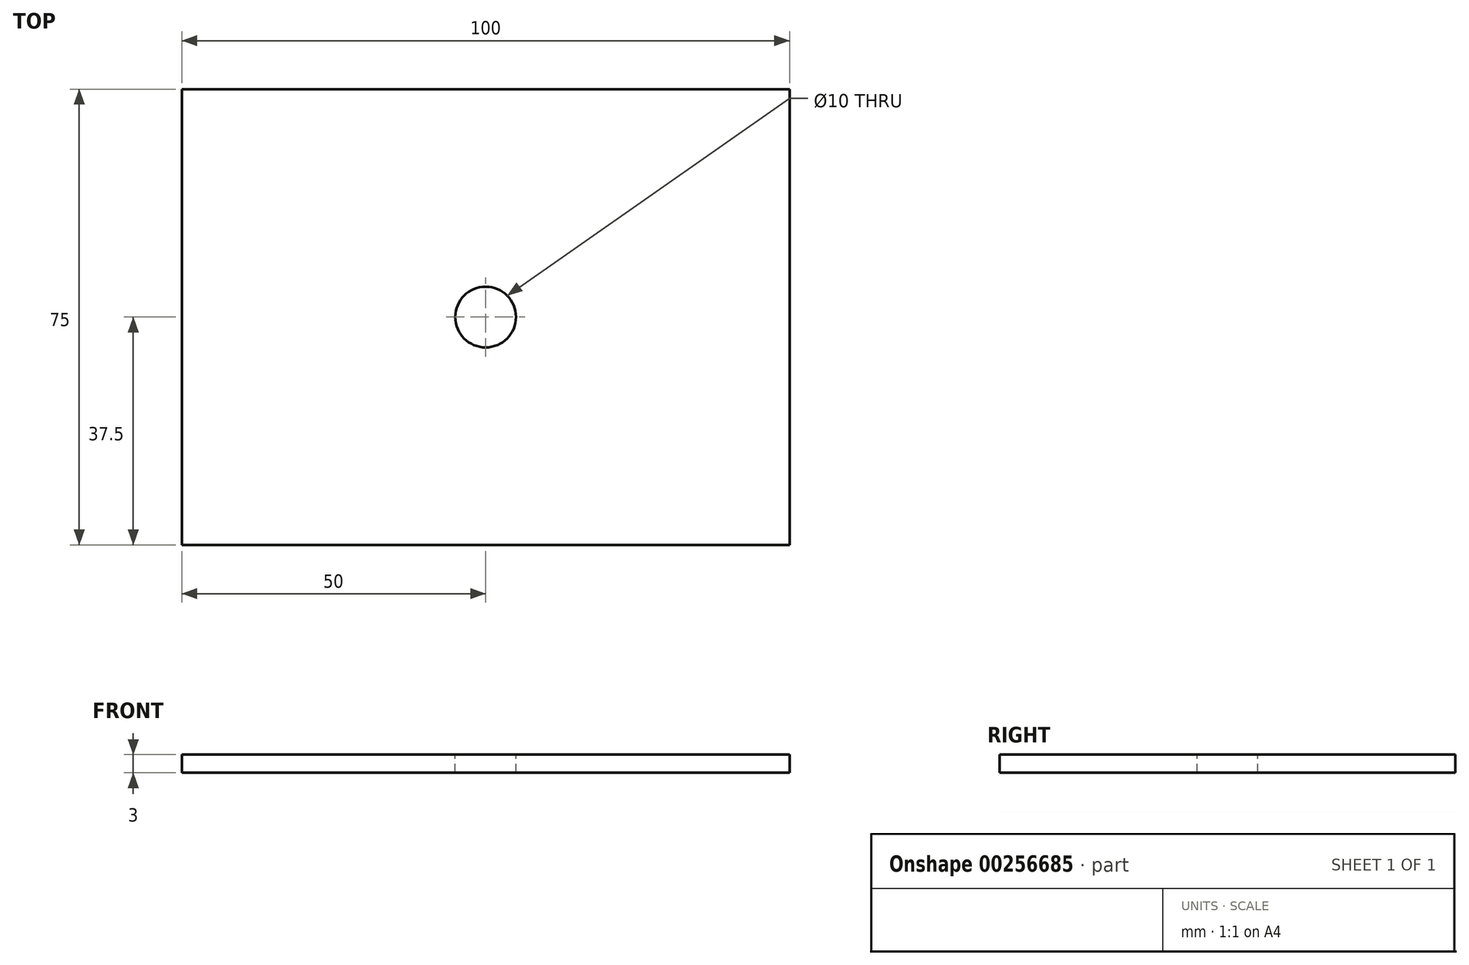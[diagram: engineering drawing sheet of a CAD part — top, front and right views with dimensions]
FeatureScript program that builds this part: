
annotation { "Feature Type Name" : "Feature", "Feature Type Description" : "" }
export const myFeature = defineFeature(function(context is Context, id is Id, definition is map)
    precondition{}
    {
        {
            var Q0;
            Q0=qCreatedBy(makeId("Top.planeOp"),FACE);
            var sketch = newSketch(context, id + "F0", { "sketchPlane" : qUnion([Q0])});
            skLineSegment(sketch, "E0.bottom", {"start": v(0, 0) * mm, "end": v(100, 0) * mm});
            skLineSegment(sketch, "E0.top", {"start": v(0, 75) * mm, "end": v(100, 75) * mm});
            skLineSegment(sketch, "E0.left", {"start": v(0, 0) * mm, "end": v(0, 75) * mm});
            skLineSegment(sketch, "E0.right", {"start": v(100, 0) * mm, "end": v(100, 75) * mm});
            skSolve(sketch);
        }
        {
            var Q0;
            Q0 = qSketchRegion(id + "F0", true);
            extrude(context, id + "F1", {"entities" : qUnion([Q0]), "depth" : 3 * mm});
        }
        {
            var Q0;
            Q0=makeQuery(id+"F1.opExtrude","CAP_FACE",FACE,{"disambiguationData":[OSD([sQuery(id+"F0.wireOp",EDGE,"E0.bottom"),sQuery(id+"F0.wireOp",EDGE,"E0.top"),sQuery(id+"F0.wireOp",EDGE,"E0.left"),sQuery(id+"F0.wireOp",EDGE,"E0.right")])],"isStart":false});
            var sketch = newSketch(context, id + "F2", { "sketchPlane" : qUnion([Q0])});
            skLineSegment(sketch, "E1.0", {"start": v(0, 0) * mm, "end": v(0, 75) * mm, "construction": true});
            skLineSegment(sketch, "E2.0", {"start": v(0, 75) * mm, "end": v(100, 75) * mm, "construction": true});
            skLineSegment(sketch, "E3.0", {"start": v(100, 0) * mm, "end": v(100, 75) * mm, "construction": true});
            skLineSegment(sketch, "E4.0", {"start": v(0, 0) * mm, "end": v(100, 0) * mm, "construction": true});
            skCircle(sketch, "E5", {"center": v(50, 37.5) * mm, "radius": 5 * mm});
            skPoint(sketch, "E6", {"position": v(0, 37.5) * mm});
            skSolve(sketch);
        }
        {
            var Q0;
            Q0 = qSketchRegion(id + "F2", true);
            extrude(context, id + "F3", {"entities" : qUnion([Q0]), "operationType" : NewBodyOperationType.REMOVE, "endBound" : BoundingType.THROUGH_ALL, "oppositeDirection" : true, "depth" : 25 * mm});
        }
    });
